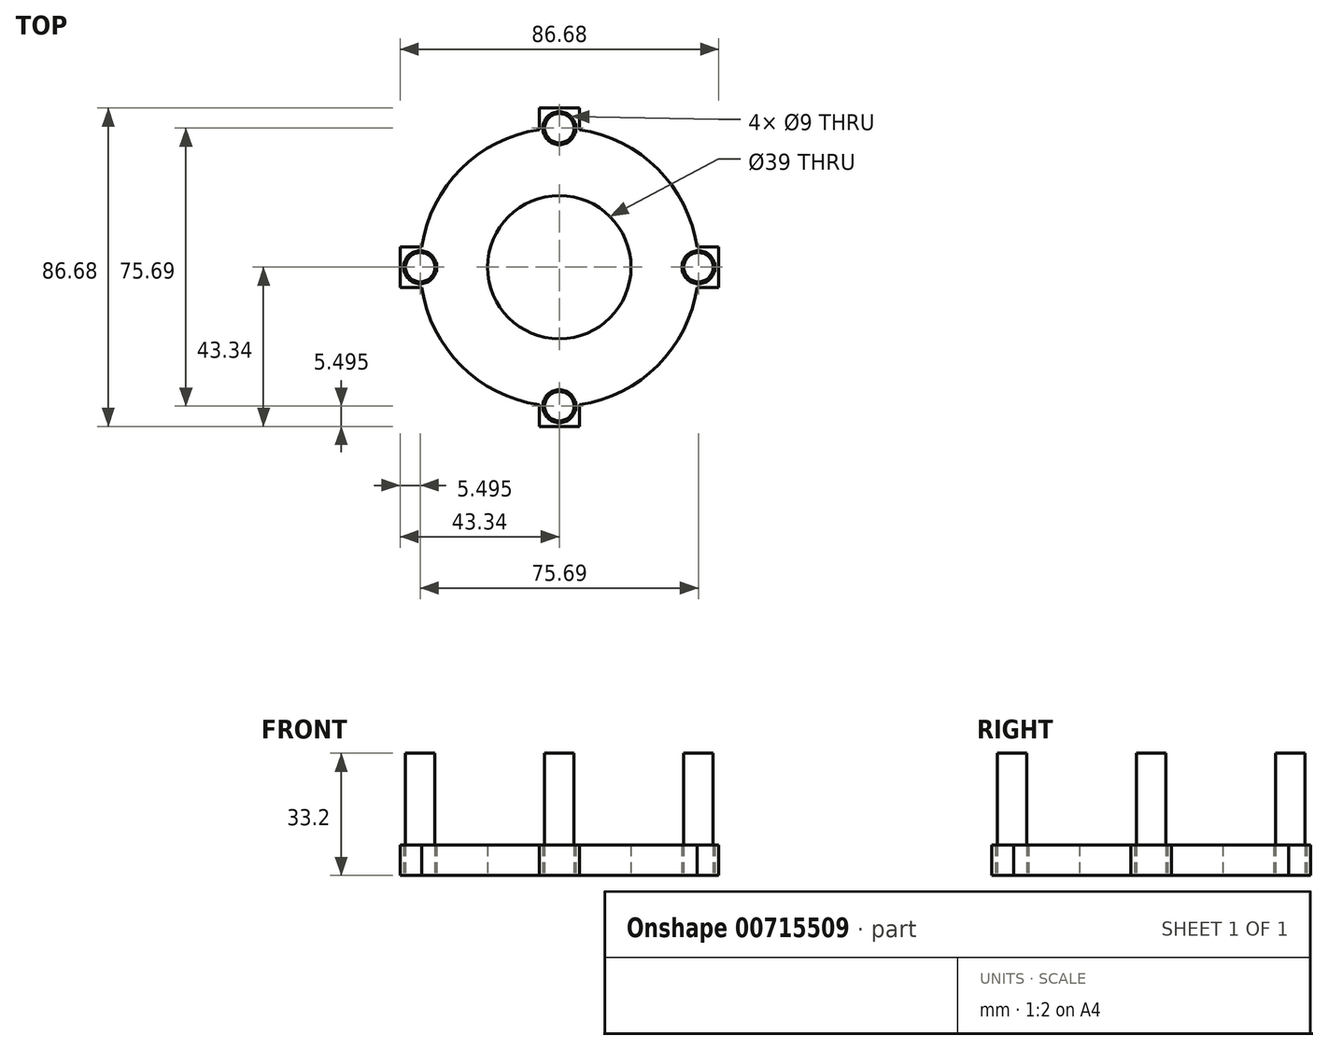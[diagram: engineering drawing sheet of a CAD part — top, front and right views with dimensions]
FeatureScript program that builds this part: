
annotation { "Feature Type Name" : "Feature", "Feature Type Description" : "" }
export const myFeature = defineFeature(function(context is Context, id is Id, definition is map)
    precondition{}
    {
        {
            var Q0;
            Q0=qCreatedBy(makeId("Top.planeOp"),FACE);
            var sketch = newSketch(context, id + "F0", { "sketchPlane" : qUnion([Q0])});
            skCircle(sketch, "E0", {"center": v(0, 0) * mm, "radius": 20 * mm});
            skCircle(sketch, "E1", {"center": v(0, 0) * mm, "radius": 37.84 * mm});
            skCircle(sketch, "E2", {"center": v(0, 37.84) * mm, "radius": 4 * mm});
            skPoint(sketch, "E3.1.0", {"position": v(-37.84, 0) * mm});
            skPoint(sketch, "E3.2.0", {"position": v(0, -37.84) * mm});
            skPoint(sketch, "E3.3.0", {"position": v(37.84, 0) * mm});
            skCircle(sketch, "E4.1.0", {"center": v(-37.84, 0) * mm, "radius": 4 * mm});
            skCircle(sketch, "E4.2.0", {"center": v(0, -37.84) * mm, "radius": 4 * mm});
            skCircle(sketch, "E4.3.0", {"center": v(37.84, 0) * mm, "radius": 4 * mm});
            skLineSegment(sketch, "E5.bottom", {"start": v(5.5, 32.34) * mm, "end": v(-5.5, 32.34) * mm});
            skLineSegment(sketch, "E5.top", {"start": v(5.5, 43.34) * mm, "end": v(-5.5, 43.34) * mm});
            skLineSegment(sketch, "E5.left", {"start": v(5.5, 32.34) * mm, "end": v(5.5, 43.34) * mm});
            skLineSegment(sketch, "E5.right", {"start": v(-5.5, 32.34) * mm, "end": v(-5.5, 43.34) * mm});
            skLineSegment(sketch, "E6.1.0", {"start": v(-32.34, 5.5) * mm, "end": v(-43.34, 5.5) * mm});
            skLineSegment(sketch, "E6.1.1", {"start": v(-43.34, 5.5) * mm, "end": v(-43.34, -5.5) * mm});
            skLineSegment(sketch, "E6.1.2", {"start": v(-32.34, -5.5) * mm, "end": v(-43.34, -5.5) * mm});
            skLineSegment(sketch, "E6.1.3", {"start": v(-32.34, 5.5) * mm, "end": v(-32.34, -5.5) * mm});
            skLineSegment(sketch, "E6.2.0", {"start": v(-5.5, -32.34) * mm, "end": v(-5.5, -43.34) * mm});
            skLineSegment(sketch, "E6.2.1", {"start": v(-5.5, -43.34) * mm, "end": v(5.5, -43.34) * mm});
            skLineSegment(sketch, "E6.2.2", {"start": v(5.5, -32.34) * mm, "end": v(5.5, -43.34) * mm});
            skLineSegment(sketch, "E6.2.3", {"start": v(-5.5, -32.34) * mm, "end": v(5.5, -32.34) * mm});
            skLineSegment(sketch, "E6.3.0", {"start": v(32.34, -5.5) * mm, "end": v(43.34, -5.5) * mm});
            skLineSegment(sketch, "E6.3.1", {"start": v(43.34, -5.5) * mm, "end": v(43.34, 5.5) * mm});
            skLineSegment(sketch, "E6.3.2", {"start": v(32.34, 5.5) * mm, "end": v(43.34, 5.5) * mm});
            skLineSegment(sketch, "E6.3.3", {"start": v(32.34, -5.5) * mm, "end": v(32.34, 5.5) * mm});
            skCircle(sketch, "E7", {"center": v(0, 37.84) * mm, "radius": 4.5 * mm});
            skCircle(sketch, "E8.1.0", {"center": v(-37.84, 0) * mm, "radius": 4.5 * mm});
            skCircle(sketch, "E8.2.0", {"center": v(0, -37.84) * mm, "radius": 4.5 * mm});
            skCircle(sketch, "E8.3.0", {"center": v(37.84, 0) * mm, "radius": 4.5 * mm});
            skCircle(sketch, "E9", {"center": v(0, 0) * mm, "radius": 28.84 * mm});
            skPoint(sketch, "E10.1.0", {"position": v(-26.76, 26.76) * mm});
            skPoint(sketch, "E10.3.0", {"position": v(-26.76, -26.76) * mm});
            skPoint(sketch, "E10.5.0", {"position": v(26.76, -26.76) * mm});
            skPoint(sketch, "E10.7.0", {"position": v(26.76, 26.76) * mm});
            skPoint(sketch, "E11", {"position": v(0, 28.84) * mm});
            skPoint(sketch, "E12.1.0", {"position": v(-20.4, 20.4) * mm});
            skPoint(sketch, "E12.2.0", {"position": v(-28.84, 0) * mm});
            skPoint(sketch, "E12.3.0", {"position": v(-20.4, -20.4) * mm});
            skPoint(sketch, "E12.4.0", {"position": v(0, -28.84) * mm});
            skPoint(sketch, "E12.5.0", {"position": v(20.4, -20.4) * mm});
            skPoint(sketch, "E12.6.0", {"position": v(28.84, 0) * mm});
            skPoint(sketch, "E12.7.0", {"position": v(20.4, 20.4) * mm});
            skCircle(sketch, "E13", {"center": v(-20.4, 20.4) * mm, "radius": 4.5 * mm});
            skCircle(sketch, "E14.1.0", {"center": v(-20.4, -20.4) * mm, "radius": 4.5 * mm});
            skCircle(sketch, "E14.2.0", {"center": v(20.4, -20.4) * mm, "radius": 4.5 * mm});
            skCircle(sketch, "E14.3.0", {"center": v(20.4, 20.4) * mm, "radius": 4.5 * mm});
            skCircle(sketch, "E15", {"center": v(0, 0) * mm, "radius": 19.5 * mm});
            skSolve(sketch);
        }
        {
            var Q0;
            Q0 = qSketchRegion(id + "F0", true);
            var Q1;
            {var subQ0=sQuery(id+"F0.wireOp",EDGE,"E4.1.0");var subQ1=sQuery(id+"F0.wireOp",EDGE,"E1");var subQ2=makeQuery(id+"F0.imprint","INTERSECT",VERTEX,{"disambiguationData":[OD(0.0)],"derivedFrom":[subQ1,subQ0]});Q1=makeQuery(id+"F0.imprint","IMPRINT",FACE,{"disambiguationData":[TD([[makeQuery(id+"F0.imprint","IMPRINT",EDGE,{"disambiguationData":[TD([[subQ2,-1.0]])],"derivedFrom":subQ1}),-1.0]])]});}
            var Q2;
            {var subQ0=sQuery(id+"F0.wireOp",EDGE,"E4.1.0");var subQ1=sQuery(id+"F0.wireOp",EDGE,"E1");var subQ2=makeQuery(id+"F0.imprint","INTERSECT",VERTEX,{"disambiguationData":[OD(0.0)],"derivedFrom":[subQ1,subQ0]});Q2=makeQuery(id+"F0.imprint","IMPRINT",FACE,{"disambiguationData":[TD([[makeQuery(id+"F0.imprint","IMPRINT",EDGE,{"disambiguationData":[TD([[subQ2,-1.0]])],"derivedFrom":subQ1}),1.0]])]});}
            var Q3;
            {var subQ0=sQuery(id+"F0.wireOp",EDGE,"E2");var subQ1=sQuery(id+"F0.wireOp",EDGE,"E1");var subQ2=makeQuery(id+"F0.imprint","INTERSECT",VERTEX,{"disambiguationData":[OD(0.0)],"derivedFrom":[subQ1,subQ0]});Q3=makeQuery(id+"F0.imprint","IMPRINT",FACE,{"disambiguationData":[TD([[makeQuery(id+"F0.imprint","IMPRINT",EDGE,{"disambiguationData":[TD([[subQ2,-1.0]])],"derivedFrom":subQ1}),-1.0]])]});}
            var Q4;
            {var subQ0=sQuery(id+"F0.wireOp",EDGE,"E2");var subQ1=sQuery(id+"F0.wireOp",EDGE,"E1");var subQ2=makeQuery(id+"F0.imprint","INTERSECT",VERTEX,{"disambiguationData":[OD(0.0)],"derivedFrom":[subQ1,subQ0]});Q4=makeQuery(id+"F0.imprint","IMPRINT",FACE,{"disambiguationData":[TD([[makeQuery(id+"F0.imprint","IMPRINT",EDGE,{"disambiguationData":[TD([[subQ2,-1.0]])],"derivedFrom":subQ1}),1.0]])]});}
            var Q5;
            {var subQ0=sQuery(id+"F0.wireOp",EDGE,"E4.3.0");var subQ1=sQuery(id+"F0.wireOp",EDGE,"E1");var subQ2=makeQuery(id+"F0.imprint","INTERSECT",VERTEX,{"disambiguationData":[OD(0.0)],"derivedFrom":[subQ1,subQ0]});Q5=makeQuery(id+"F0.imprint","IMPRINT",FACE,{"disambiguationData":[TD([[makeQuery(id+"F0.imprint","IMPRINT",EDGE,{"disambiguationData":[TD([[subQ2,1.0]])],"derivedFrom":subQ1}),1.0]])]});}
            var Q6;
            {var subQ0=sQuery(id+"F0.wireOp",EDGE,"E4.3.0");var subQ1=sQuery(id+"F0.wireOp",EDGE,"E1");var subQ2=makeQuery(id+"F0.imprint","INTERSECT",VERTEX,{"disambiguationData":[OD(0.0)],"derivedFrom":[subQ1,subQ0]});Q6=makeQuery(id+"F0.imprint","IMPRINT",FACE,{"disambiguationData":[TD([[makeQuery(id+"F0.imprint","IMPRINT",EDGE,{"disambiguationData":[TD([[subQ2,1.0]])],"derivedFrom":subQ1}),-1.0]])]});}
            var Q7;
            {var subQ0=sQuery(id+"F0.wireOp",EDGE,"E4.2.0");var subQ1=sQuery(id+"F0.wireOp",EDGE,"E1");var subQ2=makeQuery(id+"F0.imprint","INTERSECT",VERTEX,{"disambiguationData":[OD(0.0)],"derivedFrom":[subQ1,subQ0]});Q7=makeQuery(id+"F0.imprint","IMPRINT",FACE,{"disambiguationData":[TD([[makeQuery(id+"F0.imprint","IMPRINT",EDGE,{"disambiguationData":[TD([[subQ2,-1.0]])],"derivedFrom":subQ1}),1.0]])]});}
            var Q8;
            {var subQ0=sQuery(id+"F0.wireOp",EDGE,"E4.2.0");var subQ1=sQuery(id+"F0.wireOp",EDGE,"E1");var subQ2=makeQuery(id+"F0.imprint","INTERSECT",VERTEX,{"disambiguationData":[OD(0.0)],"derivedFrom":[subQ1,subQ0]});Q8=makeQuery(id+"F0.imprint","IMPRINT",FACE,{"disambiguationData":[TD([[makeQuery(id+"F0.imprint","IMPRINT",EDGE,{"disambiguationData":[TD([[subQ2,-1.0]])],"derivedFrom":subQ1}),-1.0]])]});}
            var Q9;
            {var subQ0=sQuery(id+"F0.wireOp",EDGE,"E13");var subQ1=sQuery(id+"F0.wireOp",EDGE,"E9");var subQ2=makeQuery(id+"F0.imprint","INTERSECT",VERTEX,{"disambiguationData":[OD(0.0)],"derivedFrom":[subQ1,subQ0]});Q9=makeQuery(id+"F0.imprint","IMPRINT",FACE,{"disambiguationData":[TD([[makeQuery(id+"F0.imprint","IMPRINT",EDGE,{"disambiguationData":[TD([[subQ2,-1.0]])],"derivedFrom":subQ1}),-1.0]])]});}
            var Q10;
            {var subQ0=sQuery(id+"F0.wireOp",EDGE,"E14.3.0");var subQ1=sQuery(id+"F0.wireOp",EDGE,"E9");var subQ2=makeQuery(id+"F0.imprint","INTERSECT",VERTEX,{"disambiguationData":[OD(0.0)],"derivedFrom":[subQ1,subQ0]});Q10=makeQuery(id+"F0.imprint","IMPRINT",FACE,{"disambiguationData":[TD([[makeQuery(id+"F0.imprint","IMPRINT",EDGE,{"disambiguationData":[TD([[subQ2,1.0]])],"derivedFrom":subQ1}),-1.0]])]});}
            var Q11;
            {var subQ0=sQuery(id+"F0.wireOp",EDGE,"E14.2.0");var subQ1=sQuery(id+"F0.wireOp",EDGE,"E9");var subQ2=makeQuery(id+"F0.imprint","INTERSECT",VERTEX,{"disambiguationData":[OD(0.0)],"derivedFrom":[subQ1,subQ0]});Q11=makeQuery(id+"F0.imprint","IMPRINT",FACE,{"disambiguationData":[TD([[makeQuery(id+"F0.imprint","IMPRINT",EDGE,{"disambiguationData":[TD([[subQ2,-1.0]])],"derivedFrom":subQ1}),-1.0]])]});}
            var Q12;
            {var subQ0=sQuery(id+"F0.wireOp",EDGE,"E14.1.0");var subQ1=sQuery(id+"F0.wireOp",EDGE,"E9");var subQ2=makeQuery(id+"F0.imprint","INTERSECT",VERTEX,{"disambiguationData":[OD(0.0)],"derivedFrom":[subQ1,subQ0]});Q12=makeQuery(id+"F0.imprint","IMPRINT",FACE,{"disambiguationData":[TD([[makeQuery(id+"F0.imprint","IMPRINT",EDGE,{"disambiguationData":[TD([[subQ2,-1.0]])],"derivedFrom":subQ1}),-1.0]])]});}
            var Q13;
            Q13=makeQuery(id+"F0.imprint","IMPRINT",FACE,{"disambiguationData":[TD([[makeQuery(id+"F0.imprint","IMPRINT",EDGE,{"derivedFrom":sQuery(id+"F0.wireOp",EDGE,"E0")}),-1.0]])]});
            var Q14;
            {var subQ0=sQuery(id+"F0.wireOp",EDGE,"E14.2.0");var subQ1=sQuery(id+"F0.wireOp",EDGE,"E9");var subQ2=makeQuery(id+"F0.imprint","INTERSECT",VERTEX,{"disambiguationData":[OD(0.0)],"derivedFrom":[subQ1,subQ0]});Q14=makeQuery(id+"F0.imprint","IMPRINT",FACE,{"disambiguationData":[TD([[makeQuery(id+"F0.imprint","IMPRINT",EDGE,{"disambiguationData":[TD([[subQ2,-1.0]])],"derivedFrom":subQ1}),1.0]])]});}
            var Q15;
            {var subQ0=sQuery(id+"F0.wireOp",EDGE,"E14.3.0");var subQ1=sQuery(id+"F0.wireOp",EDGE,"E9");var subQ2=makeQuery(id+"F0.imprint","INTERSECT",VERTEX,{"disambiguationData":[OD(0.0)],"derivedFrom":[subQ1,subQ0]});Q15=makeQuery(id+"F0.imprint","IMPRINT",FACE,{"disambiguationData":[TD([[makeQuery(id+"F0.imprint","IMPRINT",EDGE,{"disambiguationData":[TD([[subQ2,1.0]])],"derivedFrom":subQ1}),1.0]])]});}
            var Q16;
            {var subQ0=sQuery(id+"F0.wireOp",EDGE,"E13");var subQ1=sQuery(id+"F0.wireOp",EDGE,"E9");var subQ2=makeQuery(id+"F0.imprint","INTERSECT",VERTEX,{"disambiguationData":[OD(0.0)],"derivedFrom":[subQ1,subQ0]});Q16=makeQuery(id+"F0.imprint","IMPRINT",FACE,{"disambiguationData":[TD([[makeQuery(id+"F0.imprint","IMPRINT",EDGE,{"disambiguationData":[TD([[subQ2,-1.0]])],"derivedFrom":subQ1}),1.0]])]});}
            var Q17;
            {var subQ0=sQuery(id+"F0.wireOp",EDGE,"E14.1.0");var subQ1=sQuery(id+"F0.wireOp",EDGE,"E9");var subQ2=makeQuery(id+"F0.imprint","INTERSECT",VERTEX,{"disambiguationData":[OD(0.0)],"derivedFrom":[subQ1,subQ0]});Q17=makeQuery(id+"F0.imprint","IMPRINT",FACE,{"disambiguationData":[TD([[makeQuery(id+"F0.imprint","IMPRINT",EDGE,{"disambiguationData":[TD([[subQ2,-1.0]])],"derivedFrom":subQ1}),1.0]])]});}
            var Q18;
            Q18=makeQuery(id+"F0.imprint","IMPRINT",FACE,{"disambiguationData":[TD([[makeQuery(id+"F0.imprint","IMPRINT",EDGE,{"derivedFrom":sQuery(id+"F0.wireOp",EDGE,"E0")}),1.0]])]});
            extrude(context, id + "F1", {"entities" : qUnion([Q0, Q1, Q2, Q3, Q4, Q5, Q6, Q7, Q8, Q9, Q10, Q11, Q12, Q13, Q14, Q15, Q16, Q17, Q18]), "depth" : 8.2 * mm, "offsetDistance" : 25 * mm});
        }
        {
            var Q0;
            Q0=sQuery(id+"F0.wireOp",EDGE,"E2");
            var Q1;
            Q1=sQuery(id+"F0.wireOp",EDGE,"E4.1.0");
            var Q2;
            Q2=sQuery(id+"F0.wireOp",EDGE,"E4.3.0");
            var Q3;
            Q3=sQuery(id+"F0.wireOp",EDGE,"E4.2.0");
            var Q4;
            Q4=sQuery(id+"F0.wireOp",EDGE,"E8.1.0");
            var Q5;
            Q5=sQuery(id+"F0.wireOp",EDGE,"E7");
            var Q6;
            Q6=sQuery(id+"F0.wireOp",EDGE,"E8.3.0");
            var Q7;
            Q7=sQuery(id+"F0.wireOp",EDGE,"E8.2.0");
            extrude(context, id + "F2", {"bodyType" : ToolBodyType.SURFACE, "surfaceEntities" : qUnion([Q0, Q1, Q2, Q3, Q4, Q5, Q6, Q7]), "depth" : 20 * mm, "offsetDistance" : 25 * mm});
        }
        {
            var Q0;
            Q0=makeQuery(id+"F1.opExtrude","CAP_FACE",FACE,{"disambiguationData":[OSD([sQuery(id+"F0.wireOp",EDGE,"E2")])],"isStart":false});
            var Q1;
            Q1=makeQuery(id+"F1.opExtrude","CAP_FACE",FACE,{"disambiguationData":[OSD([sQuery(id+"F0.wireOp",EDGE,"E4.1.0")])],"isStart":false});
            var Q2;
            Q2=makeQuery(id+"F1.opExtrude","CAP_FACE",FACE,{"disambiguationData":[OSD([sQuery(id+"F0.wireOp",EDGE,"E4.3.0")])],"isStart":false});
            var Q3;
            Q3=makeQuery(id+"F1.opExtrude","CAP_FACE",FACE,{"disambiguationData":[OSD([sQuery(id+"F0.wireOp",EDGE,"E4.2.0")])],"isStart":false});
            extrude(context, id + "F3", {"entities" : qUnion([Q0, Q1, Q2, Q3]), "depth" : 25 * mm, "offsetDistance" : 25 * mm});
        }
    });
